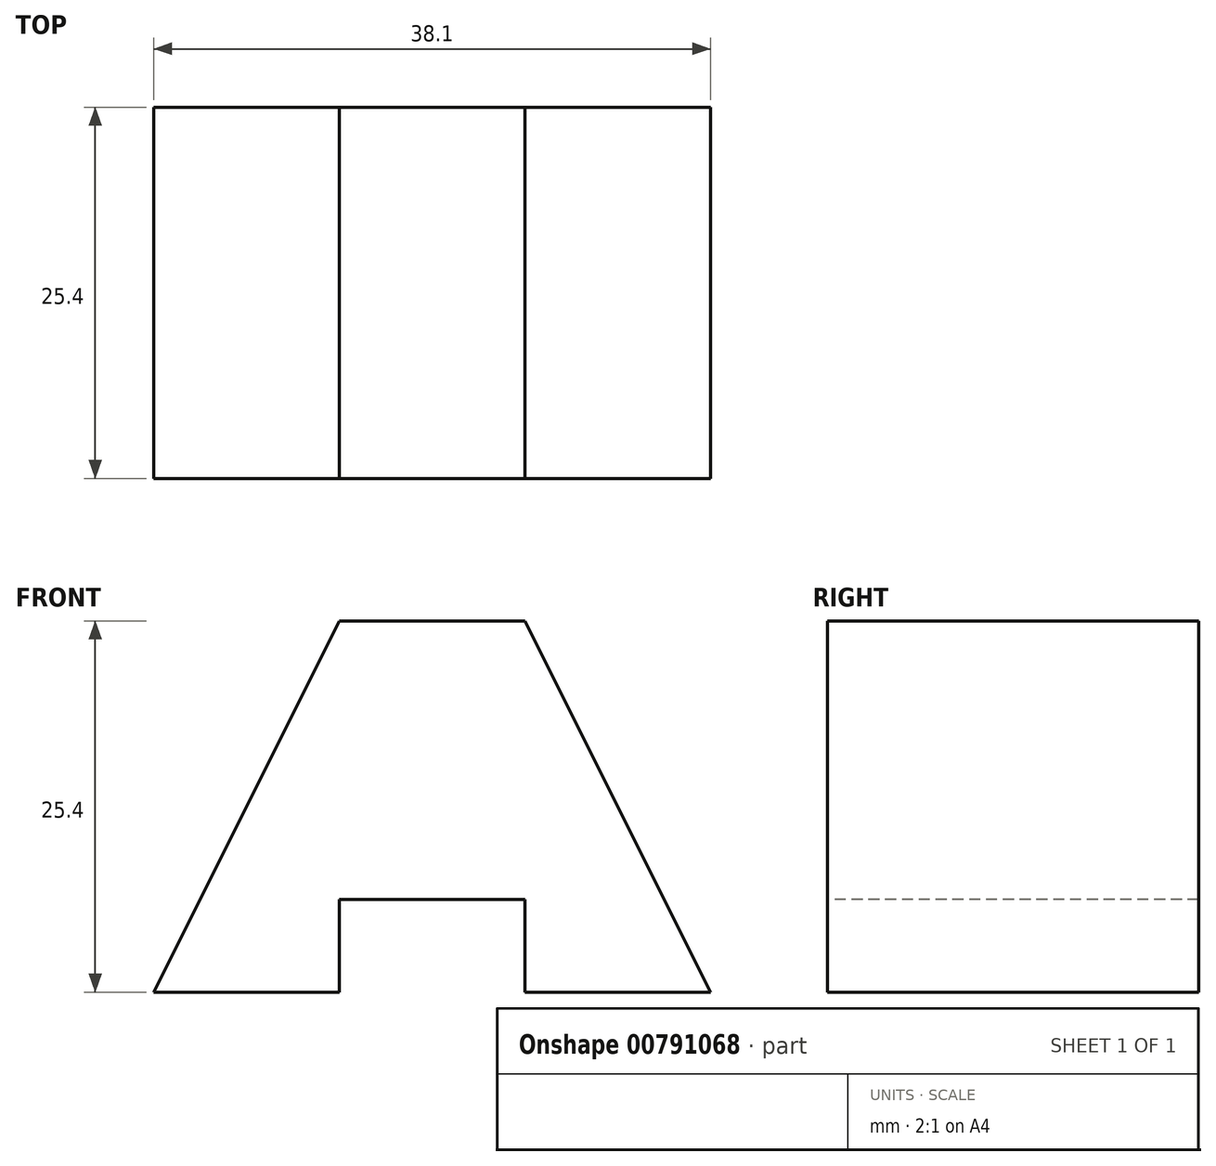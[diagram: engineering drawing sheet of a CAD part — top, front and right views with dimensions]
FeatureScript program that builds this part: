
annotation { "Feature Type Name" : "Feature", "Feature Type Description" : "" }
export const myFeature = defineFeature(function(context is Context, id is Id, definition is map)
    precondition{}
    {
        {
            var Q0;
            Q0=qCreatedBy(makeId("Front.planeOp"),FACE);
            var sketch = newSketch(context, id + "F0", { "sketchPlane" : qUnion([Q0])});
            skLineSegment(sketch, "E0", {"start": v(0, 0) * mm, "end": v(12.7, 0) * mm});
            skLineSegment(sketch, "E1", {"start": v(12.7, 0) * mm, "end": v(12.7, 6.35) * mm});
            skLineSegment(sketch, "E2", {"start": v(12.7, 6.35) * mm, "end": v(25.4, 6.35) * mm});
            skLineSegment(sketch, "E3", {"start": v(25.4, 6.35) * mm, "end": v(25.4, 0) * mm});
            skLineSegment(sketch, "E4", {"start": v(25.4, 0) * mm, "end": v(38.1, 0) * mm});
            skLineSegment(sketch, "E5", {"start": v(38.1, 0) * mm, "end": v(38.1, 25.4) * mm});
            skLineSegment(sketch, "E6", {"start": v(0, 0) * mm, "end": v(0, 25.4) * mm});
            skLineSegment(sketch, "E7", {"start": v(0, 25.4) * mm, "end": v(38.1, 25.4) * mm});
            skSolve(sketch);
        }
        {
            var Q0;
            Q0 = qSketchRegion(id + "F0", true);
            extrude(context, id + "F1", {"entities" : qUnion([Q0]), "oppositeDirection" : true, "depth" : 25.4 * mm, "offsetDistance" : 25.4 * mm});
        }
        {
            var Q0;
            Q0=makeQuery(id+"F1.opExtrude","CAP_FACE",FACE,{"disambiguationData":[OSD([sQuery(id+"F0.wireOp",EDGE,"E0"),sQuery(id+"F0.wireOp",EDGE,"E1"),sQuery(id+"F0.wireOp",EDGE,"E2"),sQuery(id+"F0.wireOp",EDGE,"E3"),sQuery(id+"F0.wireOp",EDGE,"E4"),sQuery(id+"F0.wireOp",EDGE,"E5"),sQuery(id+"F0.wireOp",EDGE,"E6"),sQuery(id+"F0.wireOp",EDGE,"E7")])],"isStart":true});
            var sketch = newSketch(context, id + "F2", { "sketchPlane" : qUnion([Q0])});
            skLineSegment(sketch, "E8", {"start": v(0, 0) * mm, "end": v(12.7, 25.4) * mm});
            skLineSegment(sketch, "E9", {"start": v(38.1, 0) * mm, "end": v(25.4, 25.4) * mm});
            skLineSegment(sketch, "E10", {"start": v(25.4, 25.4) * mm, "end": v(38.1, 25.4) * mm});
            skLineSegment(sketch, "E11", {"start": v(38.1, 25.4) * mm, "end": v(38.1, 0) * mm});
            skLineSegment(sketch, "E12", {"start": v(12.7, 25.4) * mm, "end": v(0, 25.4) * mm});
            skLineSegment(sketch, "E13", {"start": v(0, 25.4) * mm, "end": v(0, 0) * mm});
            skSolve(sketch);
        }
        {
            var Q0;
            Q0=makeQuery(id+"F2.imprint","IMPRINT",FACE,{"disambiguationData":[TD([[makeQuery(id+"F2.imprint","IMPRINT",EDGE,{"derivedFrom":sQuery(id+"F2.wireOp",EDGE,"E8")}),1.0]])]});
            var Q1;
            Q1=makeQuery(id+"F2.imprint","IMPRINT",FACE,{"disambiguationData":[TD([[makeQuery(id+"F2.imprint","IMPRINT",EDGE,{"derivedFrom":sQuery(id+"F2.wireOp",EDGE,"E9")}),-1.0]])]});
            extrude(context, id + "F3", {"entities" : qUnion([Q0, Q1]), "operationType" : NewBodyOperationType.REMOVE, "oppositeDirection" : true, "depth" : 25.4 * mm, "offsetDistance" : 25.4 * mm});
        }
    });
